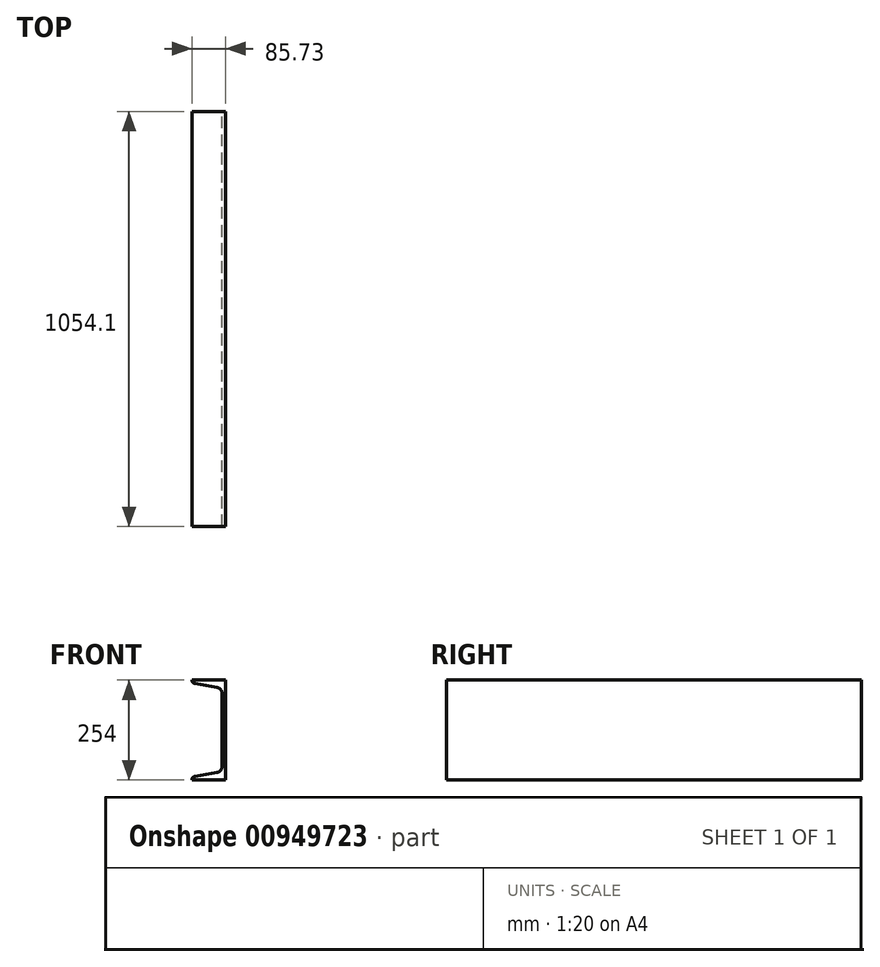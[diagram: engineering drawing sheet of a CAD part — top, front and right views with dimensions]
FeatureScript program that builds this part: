
annotation { "Feature Type Name" : "Feature", "Feature Type Description" : "" }
export const myFeature = defineFeature(function(context is Context, id is Id, definition is map)
    precondition{}
    {
        {
            var Q0;
            Q0=qCreatedBy(makeId("Front.planeOp"),FACE);
            var sketch = newSketch(context, id + "F0", { "sketchPlane" : qUnion([Q0])});
            skLineSegment(sketch, "E0", {"start": v(0, 127) * mm, "end": v(0, -127) * mm});
            skLineSegment(sketch, "E1", {"start": v(0, -127) * mm, "end": v(-85.73, -127) * mm});
            skLineSegment(sketch, "E2", {"start": v(0, 127) * mm, "end": v(-85.72, 127) * mm});
            skLineSegment(sketch, "E3", {"start": v(-9.53, 93.66) * mm, "end": v(-9.53, -93.66) * mm});
            skArc(sketch, "E4", {"start": v(-78.17, -118) * mm, "mid": v(-83.59, -121.13) * mm, "end": v(-85.73, -127) * mm});
            skArc(sketch, "E5", {"start": v(-85.73, 127) * mm, "mid": v(-83.59, 121.13) * mm, "end": v(-78.17, 118) * mm});
            skArc(sketch, "E6", {"start": v(-21.6, -108.06) * mm, "mid": v(-12.95, -103.06) * mm, "end": v(-9.53, -93.66) * mm});
            skArc(sketch, "E7", {"start": v(-9.53, 93.66) * mm, "mid": v(-12.95, 103.06) * mm, "end": v(-21.6, 108.06) * mm});
            skLineSegment(sketch, "E8", {"start": v(-78.17, -118) * mm, "end": v(-21.6, -108.06) * mm});
            skLineSegment(sketch, "E9", {"start": v(-78.17, 118) * mm, "end": v(-21.6, 108.06) * mm});
            skSolve(sketch);
        }
        {
            var Q0;
            Q0=qSketchRegion(id+"F0",true);
            extrude(context, id + "F1", {"entities" : qUnion([Q0]), "depth" : 1054.1 * mm, "offsetDistance" : 25.4 * mm});
        }
    });
